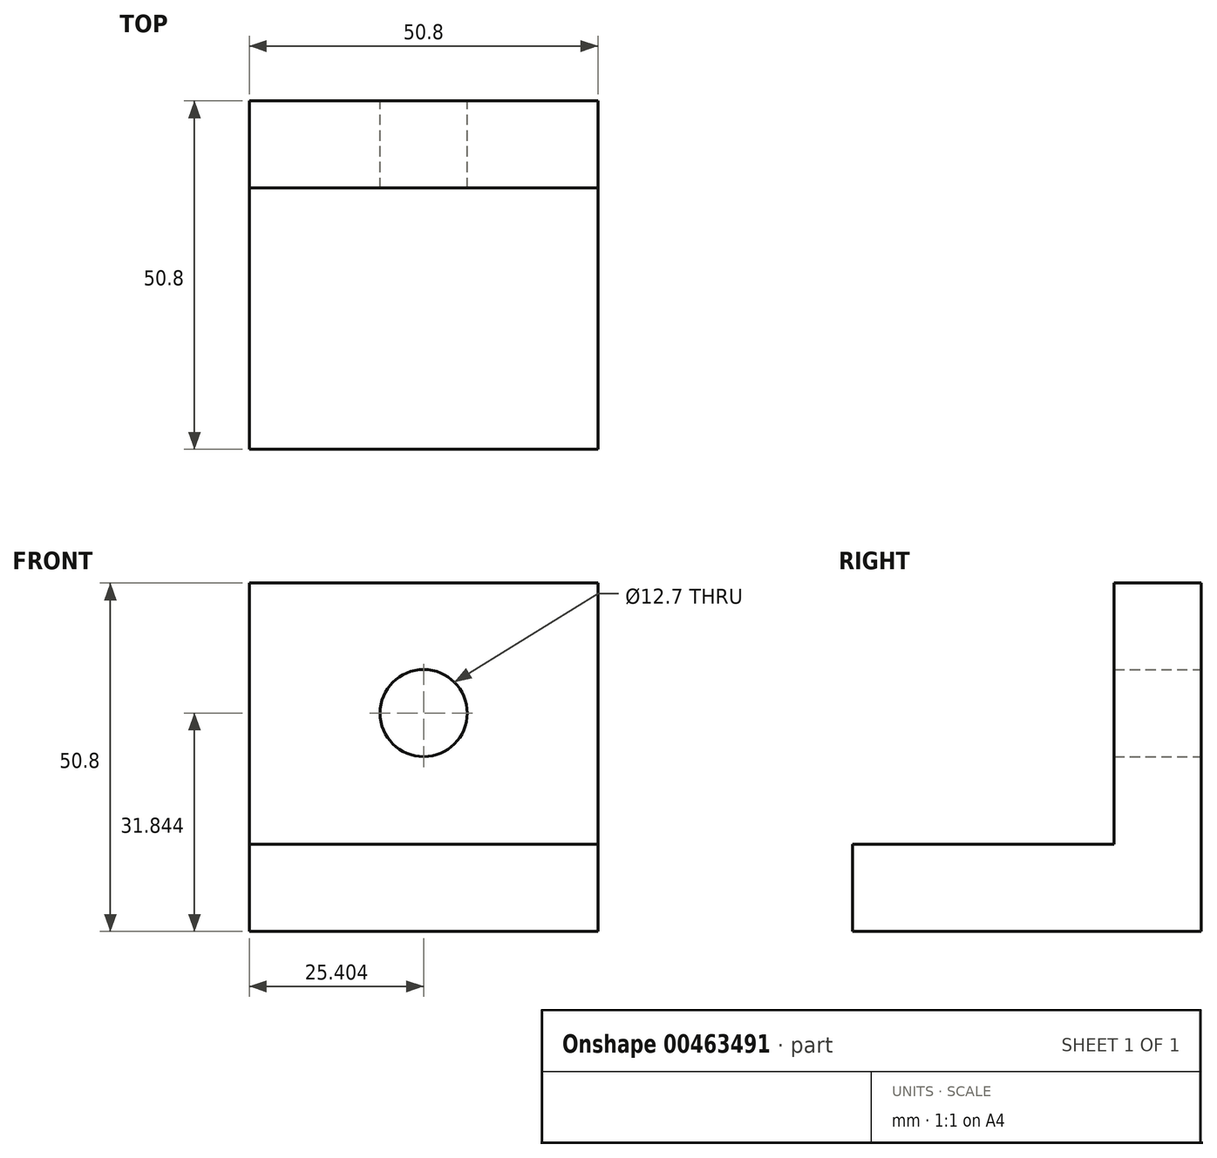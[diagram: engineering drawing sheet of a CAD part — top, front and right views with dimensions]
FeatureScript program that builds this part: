
annotation { "Feature Type Name" : "Feature", "Feature Type Description" : "" }
export const myFeature = defineFeature(function(context is Context, id is Id, definition is map)
    precondition{}
    {
        {
            var Q0;
            Q0=qCreatedBy(makeId("Front.planeOp"),FACE);
            var sketch = newSketch(context, id + "F0", { "sketchPlane" : qUnion([Q0])});
            skLineSegment(sketch, "E0.bottom", {"start": v(-5.75, 8.34) * mm, "end": v(45.05, 8.34) * mm});
            skLineSegment(sketch, "E0.top", {"start": v(-5.75, -42.46) * mm, "end": v(45.05, -42.46) * mm});
            skLineSegment(sketch, "E0.left", {"start": v(-5.75, 8.34) * mm, "end": v(-5.75, -42.46) * mm});
            skLineSegment(sketch, "E0.right", {"start": v(45.05, 8.34) * mm, "end": v(45.05, -42.46) * mm});
            skLineSegment(sketch, "E1", {"start": v(-5.75, -29.76) * mm, "end": v(45.05, -29.76) * mm});
            skCircle(sketch, "E2", {"center": v(19.65, -10.62) * mm, "radius": 6.35 * mm});
            skPoint(sketch, "E3", {"position": v(19.65, 8.34) * mm});
            skSolve(sketch);
        }
        {
            var Q0;
            {var subQ0=sQuery(id+"F0.wireOp",EDGE,"E0.top");Q0=makeQuery(id+"F0.imprint","IMPRINT",FACE,{"disambiguationData":[TD([[makeQuery(id+"F0.imprint","IMPRINT",EDGE,{"derivedFrom":subQ0}),1.0]])]});}
            extrude(context, id + "F1", {"entities" : qUnion([Q0]), "depth" : 50.8 * mm});
        }
        {
            var Q0;
            Q0 = qSketchRegion(id + "F0", true);
            extrude(context, id + "F2", {"entities" : qUnion([Q0]), "operationType" : NewBodyOperationType.ADD, "depth" : 12.7 * mm});
        }
    });
